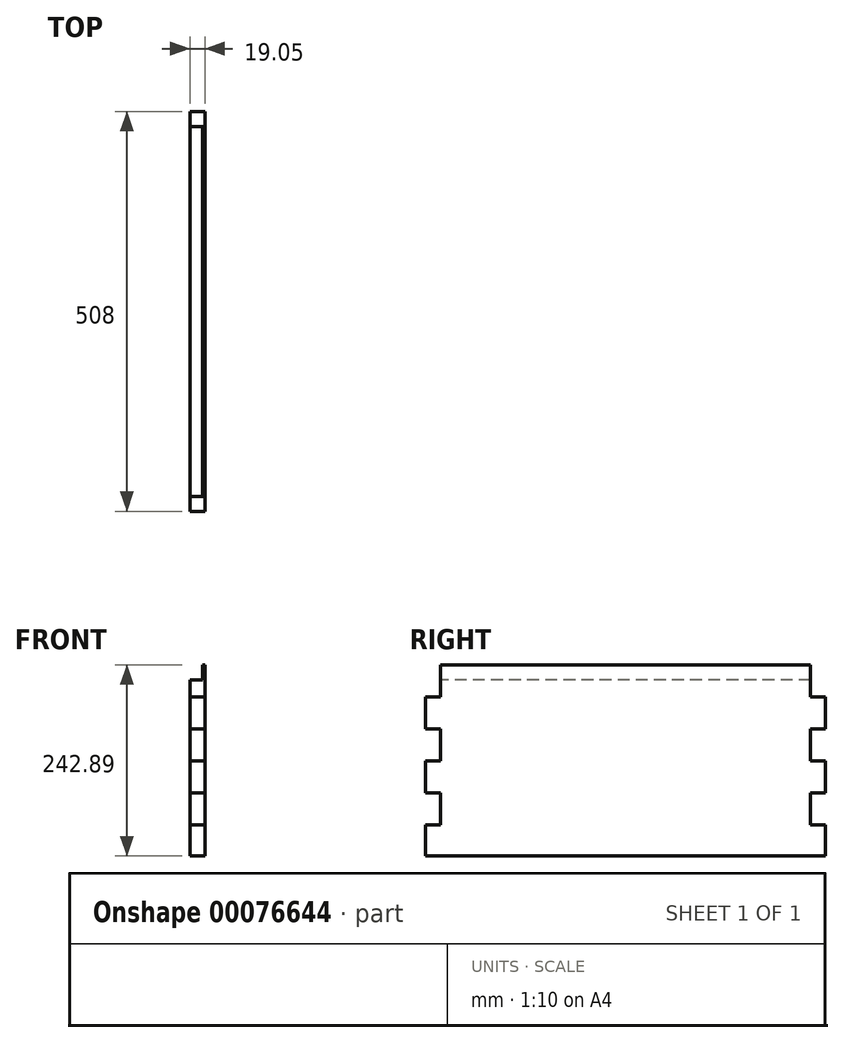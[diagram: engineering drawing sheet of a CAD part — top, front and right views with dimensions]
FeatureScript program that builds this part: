
annotation { "Feature Type Name" : "Feature", "Feature Type Description" : "" }
export const myFeature = defineFeature(function(context is Context, id is Id, definition is map)
    precondition{}
    {
        {
            var Q0;
            Q0=qCreatedBy(makeId("Right.planeOp"),FACE);
            var sketch = newSketch(context, id + "F0", { "sketchPlane" : qUnion([Q0])});
            skLineSegment(sketch, "E0.bottom", {"start": v(-257.36, 120.4) * mm, "end": v(250.64, 120.4) * mm});
            skLineSegment(sketch, "E0.top", {"start": v(-257.36, -122.49) * mm, "end": v(250.64, -122.49) * mm});
            skLineSegment(sketch, "E0.left", {"start": v(-257.36, 120.4) * mm, "end": v(-257.36, -122.49) * mm});
            skLineSegment(sketch, "E0.right", {"start": v(250.64, 120.4) * mm, "end": v(250.64, -122.49) * mm});
            skSolve(sketch);
        }
        {
            var Q0;
            Q0=makeQuery(id+"F0.imprint","IMPRINT",FACE,{"disambiguationData":[TD([[makeQuery(id+"F0.imprint","IMPRINT",EDGE,{"derivedFrom":sQuery(id+"F0.wireOp",EDGE,"E0.bottom")}),-1.0]])]});
            extrude(context, id + "F1", {"entities" : qUnion([Q0]), "depth" : 19.05 * mm});
        }
        {
            var Q0;
            Q0=makeQuery(id+"F1.opExtrude","CAP_FACE",FACE,{"disambiguationData":[OSD([sQuery(id+"F0.wireOp",EDGE,"E0.bottom"),sQuery(id+"F0.wireOp",EDGE,"E0.top"),sQuery(id+"F0.wireOp",EDGE,"E0.left"),sQuery(id+"F0.wireOp",EDGE,"E0.right")])],"isStart":false});
            var sketch = newSketch(context, id + "F2", { "sketchPlane" : qUnion([Q0])});
            skLineSegment(sketch, "E1.bottom", {"start": v(-257.36, 120.4) * mm, "end": v(-238.3, 120.4) * mm});
            skLineSegment(sketch, "E1.top", {"start": v(-257.36, 79.76) * mm, "end": v(-238.3, 79.76) * mm});
            skLineSegment(sketch, "E1.left", {"start": v(-257.36, 120.4) * mm, "end": v(-257.36, 79.76) * mm});
            skLineSegment(sketch, "E1.right", {"start": v(-238.3, 120.4) * mm, "end": v(-238.3, 79.76) * mm});
            skLineSegment(sketch, "E2.top", {"start": v(-257.36, 39.12) * mm, "end": v(-238.3, 39.12) * mm});
            skLineSegment(sketch, "E2.left", {"start": v(-257.36, 79.76) * mm, "end": v(-257.36, 39.12) * mm});
            skLineSegment(sketch, "E2.right", {"start": v(-238.3, 79.76) * mm, "end": v(-238.3, 39.12) * mm});
            skLineSegment(sketch, "E3.top", {"start": v(-257.36, -1.52) * mm, "end": v(-238.3, -1.52) * mm});
            skLineSegment(sketch, "E3.left", {"start": v(-257.36, 39.12) * mm, "end": v(-257.36, -1.52) * mm});
            skLineSegment(sketch, "E3.right", {"start": v(-238.3, 39.12) * mm, "end": v(-238.3, -1.52) * mm});
            skLineSegment(sketch, "E4.top", {"start": v(-257.36, -42.16) * mm, "end": v(-238.3, -42.16) * mm});
            skLineSegment(sketch, "E4.left", {"start": v(-257.36, -1.52) * mm, "end": v(-257.36, -42.16) * mm});
            skLineSegment(sketch, "E4.right", {"start": v(-238.3, -1.52) * mm, "end": v(-238.3, -42.16) * mm});
            skLineSegment(sketch, "E5.top", {"start": v(-257.36, -82.8) * mm, "end": v(-238.3, -82.8) * mm});
            skLineSegment(sketch, "E5.left", {"start": v(-257.36, -42.16) * mm, "end": v(-257.36, -82.8) * mm});
            skLineSegment(sketch, "E5.right", {"start": v(-238.3, -42.16) * mm, "end": v(-238.3, -82.8) * mm});
            skLineSegment(sketch, "E6.top", {"start": v(-257.36, -122.49) * mm, "end": v(-238.3, -122.49) * mm});
            skLineSegment(sketch, "E6.left", {"start": v(-257.36, -82.8) * mm, "end": v(-257.36, -122.49) * mm});
            skLineSegment(sketch, "E6.right", {"start": v(-238.3, -82.8) * mm, "end": v(-238.3, -122.49) * mm});
            skLineSegment(sketch, "E7", {"start": v(-3.36, 120.4) * mm, "end": v(-3.36, -122.49) * mm, "construction": true});
            skLineSegment(sketch, "E8.MirrorCS", {"start": v(250.64, -82.8) * mm, "end": v(231.6, -82.8) * mm});
            skLineSegment(sketch, "E9.MirrorCS", {"start": v(250.64, 39.12) * mm, "end": v(231.6, 39.12) * mm});
            skLineSegment(sketch, "E10.MirrorCS", {"start": v(250.64, 79.76) * mm, "end": v(231.6, 79.76) * mm});
            skLineSegment(sketch, "E11.MirrorCS", {"start": v(250.64, -1.52) * mm, "end": v(231.6, -1.52) * mm});
            skLineSegment(sketch, "E12.MirrorCS", {"start": v(250.64, -42.16) * mm, "end": v(231.6, -42.16) * mm});
            skLineSegment(sketch, "E13.MirrorCS", {"start": v(250.64, -82.8) * mm, "end": v(250.64, -122.49) * mm});
            skLineSegment(sketch, "E14.MirrorCS", {"start": v(250.64, 120.4) * mm, "end": v(250.64, 79.76) * mm});
            skLineSegment(sketch, "E15.MirrorCS", {"start": v(250.64, -122.49) * mm, "end": v(231.6, -122.49) * mm});
            skLineSegment(sketch, "E16.MirrorCS", {"start": v(250.64, -1.52) * mm, "end": v(250.64, -42.16) * mm});
            skLineSegment(sketch, "E17.MirrorCS", {"start": v(250.64, 120.4) * mm, "end": v(231.6, 120.4) * mm});
            skLineSegment(sketch, "E18.MirrorCS", {"start": v(250.64, 39.12) * mm, "end": v(250.64, -1.52) * mm});
            skLineSegment(sketch, "E19.MirrorCS", {"start": v(231.6, 79.76) * mm, "end": v(231.6, 39.12) * mm});
            skLineSegment(sketch, "E20.MirrorCS", {"start": v(250.64, 79.76) * mm, "end": v(250.64, 39.12) * mm});
            skLineSegment(sketch, "E21.MirrorCS", {"start": v(231.6, -42.16) * mm, "end": v(231.6, -82.8) * mm});
            skLineSegment(sketch, "E22.MirrorCS", {"start": v(231.6, -1.52) * mm, "end": v(231.6, -42.16) * mm});
            skLineSegment(sketch, "E23.MirrorCS", {"start": v(231.6, 39.12) * mm, "end": v(231.6, -1.52) * mm});
            skLineSegment(sketch, "E24.MirrorCS", {"start": v(231.6, -82.8) * mm, "end": v(231.6, -122.49) * mm});
            skLineSegment(sketch, "E25.MirrorCS", {"start": v(250.64, -42.16) * mm, "end": v(250.64, -82.8) * mm});
            skLineSegment(sketch, "E26.MirrorCS", {"start": v(231.6, 120.4) * mm, "end": v(231.6, 79.76) * mm});
            skSolve(sketch);
        }
        {
            var Q0;
            Q0=makeQuery(id+"F2.imprint","IMPRINT",FACE,{"disambiguationData":[TD([[makeQuery(id+"F2.imprint","IMPRINT",EDGE,{"derivedFrom":sQuery(id+"F2.wireOp",EDGE,"E14.MirrorCS")}),-1.0]])]});
            var Q1;
            Q1=makeQuery(id+"F2.imprint","IMPRINT",FACE,{"disambiguationData":[TD([[makeQuery(id+"F2.imprint","IMPRINT",EDGE,{"derivedFrom":sQuery(id+"F2.wireOp",EDGE,"E18.MirrorCS")}),-1.0]])]});
            var Q2;
            Q2=makeQuery(id+"F2.imprint","IMPRINT",FACE,{"disambiguationData":[TD([[makeQuery(id+"F2.imprint","IMPRINT",EDGE,{"derivedFrom":sQuery(id+"F2.wireOp",EDGE,"E8.MirrorCS")}),-1.0]])]});
            var Q3;
            Q3=makeQuery(id+"F2.imprint","IMPRINT",FACE,{"disambiguationData":[TD([[makeQuery(id+"F2.imprint","IMPRINT",EDGE,{"derivedFrom":sQuery(id+"F2.wireOp",EDGE,"E4.top")}),-1.0]])]});
            var Q4;
            Q4=makeQuery(id+"F2.imprint","IMPRINT",FACE,{"disambiguationData":[TD([[makeQuery(id+"F2.imprint","IMPRINT",EDGE,{"derivedFrom":sQuery(id+"F2.wireOp",EDGE,"E2.top")}),-1.0]])]});
            var Q5;
            Q5=makeQuery(id+"F2.imprint","IMPRINT",FACE,{"disambiguationData":[TD([[makeQuery(id+"F2.imprint","IMPRINT",EDGE,{"derivedFrom":sQuery(id+"F2.wireOp",EDGE,"E1.bottom")}),-1.0]])]});
            extrude(context, id + "F3", {"entities" : qUnion([Q0, Q1, Q2, Q3, Q4, Q5]), "operationType" : NewBodyOperationType.REMOVE, "oppositeDirection" : true, "depth" : 25.4 * mm});
        }
        {
            var Q0;
            Q0=makeQuery(id+"F1.opExtrude","CAP_FACE",FACE,{"disambiguationData":[OSD([sQuery(id+"F0.wireOp",EDGE,"E0.bottom"),sQuery(id+"F0.wireOp",EDGE,"E0.top"),sQuery(id+"F0.wireOp",EDGE,"E0.left"),sQuery(id+"F0.wireOp",EDGE,"E0.right")])],"isStart":true});
            var sketch = newSketch(context, id + "F4", { "sketchPlane" : qUnion([Q0])});
            skLineSegment(sketch, "E27", {"start": v(-231.6, 120.4) * mm, "end": v(-231.6, 101.35) * mm, "construction": true});
            skLineSegment(sketch, "E28", {"start": v(-231.6, 101.35) * mm, "end": v(238.3, 101.35) * mm});
            skLineSegment(sketch, "E29", {"start": v(238.3, 101.35) * mm, "end": v(238.3, 120.4) * mm});
            skLineSegment(sketch, "E30", {"start": v(238.3, 120.4) * mm, "end": v(-231.6, 120.4) * mm});
            skSolve(sketch);
        }
        {
            var Q0;
            Q0 = qSketchRegion(id + "F4", true);
            var Q1;
            {var subQ0=sQuery(id+"F4.wireOp",EDGE,"E28");Q1=makeQuery(id+"F4.imprint","IMPRINT",FACE,{"disambiguationData":[TD([[makeQuery(id+"F4.imprint","IMPRINT",EDGE,{"derivedFrom":subQ0}),1.0]])]});}
            extrude(context, id + "F5", {"entities" : qUnion([Q0, Q1]), "operationType" : NewBodyOperationType.REMOVE, "oppositeDirection" : true, "depth" : 15.88 * mm});
        }
    });
